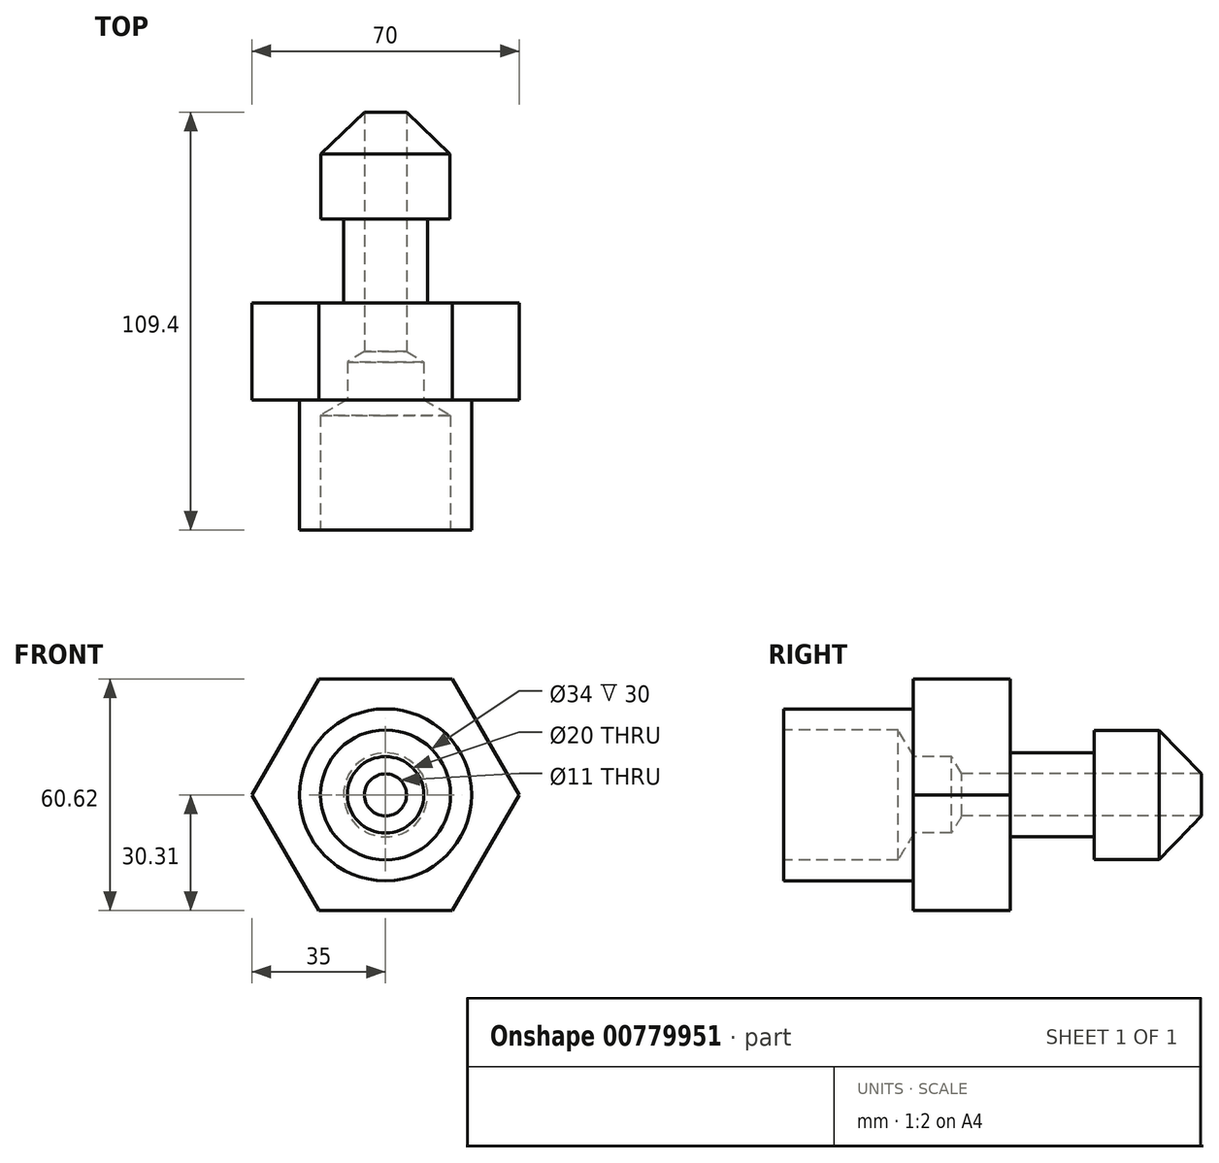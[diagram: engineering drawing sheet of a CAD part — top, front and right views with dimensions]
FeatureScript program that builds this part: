
annotation { "Feature Type Name" : "Feature", "Feature Type Description" : "" }
export const myFeature = defineFeature(function(context is Context, id is Id, definition is map)
    precondition{}
    {
        {
            var Q0;
            Q0=qCreatedBy(makeId("Front.planeOp"),FACE);
            var sketch = newSketch(context, id + "F0", { "sketchPlane" : qUnion([Q0])});
            skCircle(sketch, "E0", {"center": v(0, 0) * mm, "radius": 5.5 * mm});
            skSolve(sketch);
        }
        {
            var Q0;
            Q0=makeQuery(id+"F0.imprint","IMPRINT",FACE,{"disambiguationData":[TD([[makeQuery(id+"F0.imprint","IMPRINT",EDGE,{"derivedFrom":sQuery(id+"F0.wireOp",EDGE,"E0")}),1.0]])]});
            extrude(context, id + "F1", {"entities" : qUnion([Q0]), "depth" : 11 * mm, "offsetDistance" : 25.4 * mm, "hasDraft" : true, "draftAngle" : 46 * degree});
        }
        {
            var Q0;
            Q0=makeQuery(id+"F1.opExtrude","CAP_FACE",FACE,{"disambiguationData":[OSD([sQuery(id+"F0.wireOp",EDGE,"E0")])],"isStart":false});
            var sketch = newSketch(context, id + "F2", { "sketchPlane" : qUnion([Q0])});
            skCircle(sketch, "E1", {"center": v(0, 0) * mm, "radius": 17 * mm});
            skSolve(sketch);
        }
        {
            var Q0;
            Q0=makeQuery(id+"F2.imprint","IMPRINT",FACE,{"disambiguationData":[TD([[makeQuery(id+"F2.imprint","IMPRINT",EDGE,{"derivedFrom":makeQuery(id+"F1.opExtrude","CAP_EDGE",EDGE,{"disambiguationData":[OSD([sQuery(id+"F0.wireOp",EDGE,"E0")])],"isStart":false})}),1.0]])]});
            extrude(context, id + "F3", {"entities" : qUnion([Q0]), "operationType" : NewBodyOperationType.ADD, "depth" : 17 * mm, "offsetDistance" : 25.4 * mm});
        }
        {
            var Q0;
            Q0=makeQuery(id+"F3.opExtrude","CAP_FACE",FACE,{"disambiguationData":[OSD([sQuery(id+"F0.wireOp",EDGE,"E0")])],"isStart":false});
            var sketch = newSketch(context, id + "F4", { "sketchPlane" : qUnion([Q0])});
            skCircle(sketch, "E2", {"center": v(0, 0) * mm, "radius": 11 * mm});
            skSolve(sketch);
        }
        {
            var Q0;
            Q0=makeQuery(id+"F4.imprint","IMPRINT",FACE,{"disambiguationData":[TD([[makeQuery(id+"F4.imprint","IMPRINT",EDGE,{"derivedFrom":sQuery(id+"F4.wireOp",EDGE,"E2")}),1.0]])]});
            extrude(context, id + "F5", {"entities" : qUnion([Q0]), "operationType" : NewBodyOperationType.ADD, "depth" : 22 * mm, "offsetDistance" : 25.4 * mm});
        }
        {
            var Q0;
            Q0=makeQuery(id+"F5.opExtrude","CAP_FACE",FACE,{"disambiguationData":[OSD([sQuery(id+"F4.wireOp",EDGE,"E2")])],"isStart":false});
            var sketch = newSketch(context, id + "F6", { "sketchPlane" : qUnion([Q0])});
            skCircle(sketch, "E3.cCircle", {"center": v(0, 0) * mm, "radius": 30.31 * mm, "construction": true});
            skLineSegment(sketch, "E3.0", {"start": v(35, 0) * mm, "end": v(17.5, -30.31) * mm});
            skLineSegment(sketch, "E3.1", {"start": v(17.5, -30.31) * mm, "end": v(-17.5, -30.31) * mm});
            skLineSegment(sketch, "E3.2", {"start": v(-17.5, -30.31) * mm, "end": v(-35, 0) * mm});
            skLineSegment(sketch, "E3.3", {"start": v(-35, 0) * mm, "end": v(-17.5, 30.31) * mm});
            skLineSegment(sketch, "E3.4", {"start": v(-17.5, 30.31) * mm, "end": v(17.5, 30.31) * mm});
            skLineSegment(sketch, "E3.5", {"start": v(17.5, 30.31) * mm, "end": v(35, 0) * mm});
            skPoint(sketch, "E3.0.midPoint", {"position": v(26.25, -15.16) * mm});
            skSolve(sketch);
        }
        {
            var Q0;
            Q0=makeQuery(id+"F6.imprint","IMPRINT",FACE,{"disambiguationData":[TD([[makeQuery(id+"F6.imprint","IMPRINT",EDGE,{"derivedFrom":sQuery(id+"F6.wireOp",EDGE,"E3.0")}),-1.0]])]});
            var Q1;
            Q1=makeQuery(id+"F6.imprint","IMPRINT",FACE,{"disambiguationData":[TD([[makeQuery(id+"F6.imprint","IMPRINT",EDGE,{"derivedFrom":makeQuery(id+"F5.opExtrude","CAP_EDGE",EDGE,{"disambiguationData":[OSD([sQuery(id+"F4.wireOp",EDGE,"E2")])],"isStart":false})}),1.0]])]});
            extrude(context, id + "F7", {"entities" : qUnion([Q0, Q1]), "operationType" : NewBodyOperationType.ADD, "depth" : 25.4 * mm, "offsetDistance" : 25.4 * mm});
        }
        {
            var Q0;
            Q0=makeQuery(id+"F7.opExtrude","CAP_FACE",FACE,{"disambiguationData":[OSD([sQuery(id+"F6.wireOp",EDGE,"E3.0"),sQuery(id+"F6.wireOp",EDGE,"E3.1"),sQuery(id+"F6.wireOp",EDGE,"E3.2"),sQuery(id+"F6.wireOp",EDGE,"E3.3"),sQuery(id+"F6.wireOp",EDGE,"E3.4"),sQuery(id+"F6.wireOp",EDGE,"E3.5")])],"isStart":false});
            var sketch = newSketch(context, id + "F8", { "sketchPlane" : qUnion([Q0])});
            skCircle(sketch, "E4", {"center": v(0, 0) * mm, "radius": 22.5 * mm});
            skCircle(sketch, "E5", {"center": v(0, 0) * mm, "radius": 5.5 * mm});
            skSolve(sketch);
        }
        {
            var Q0;
            Q0=makeQuery(id+"F8.imprint","IMPRINT",FACE,{"disambiguationData":[TD([[makeQuery(id+"F8.imprint","IMPRINT",EDGE,{"derivedFrom":sQuery(id+"F8.wireOp",EDGE,"E4")}),1.0]])]});
            var Q1;
            Q1=makeQuery(id+"F8.imprint","IMPRINT",FACE,{"disambiguationData":[TD([[makeQuery(id+"F8.imprint","IMPRINT",EDGE,{"derivedFrom":sQuery(id+"F8.wireOp",EDGE,"E5")}),1.0]])]});
            extrude(context, id + "F9", {"entities" : qUnion([Q0, Q1]), "operationType" : NewBodyOperationType.ADD, "depth" : 34 * mm, "offsetDistance" : 25.4 * mm, "hasDraft" : true, "draftAngle" : 0 * degree});
        }
        {
            var Q0;
            Q0=makeQuery(id+"F9.opExtrude","CAP_FACE",FACE,{"disambiguationData":[OSD([sQuery(id+"F8.wireOp",EDGE,"E4")])],"isStart":false});
            var sketch = newSketch(context, id + "F10", { "sketchPlane" : qUnion([Q0])});
            skCircle(sketch, "E6", {"center": v(0, 0) * mm, "radius": 17 * mm});
            skSolve(sketch);
        }
        {
            var Q0;
            Q0=sQuery(id+"F10.wireOp",VERTEX,"E6.center");
            var Q1;
            Q1=makeQuery(id+"F1.opExtrude","SWEPT_BODY",BODY,{"disambiguationData":[OSD([sQuery(id+"F0.wireOp",EDGE,"E0")])]});
            hole(context, id + "F11", {"style" : HoleStyle.SIMPLE, "endStyle" : HoleEndStyle.BLIND, "standardTappedOrClearance" : lookupTablePath({ "standard" : "ISO", "size" : "34", "type" : "Drilled" }), "standardBlindInLast" : lookupTablePath({ "standard" : "ISO", "size" : "34", "type" : "Drilled" }), "holeDiameter" : 34 * mm, "majorDiameter" : 6.35 * mm, "holeDepth" : 30 * mm, "isTappedThrough" : true, "tappedDepth" : 12.7 * mm, "tapClearance" : 3, "locations" : qUnion([Q0]), "scope" : qUnion([Q1])});
        }
        {
            var Q0;
            Q0=sQuery(id+"F10.wireOp",VERTEX,"E6.center");
            var Q1;
            Q1=makeQuery(id+"F1.opExtrude","SWEPT_BODY",BODY,{"disambiguationData":[OSD([sQuery(id+"F0.wireOp",EDGE,"E0")])]});
            hole(context, id + "F12", {"style" : HoleStyle.C_SINK, "endStyle" : HoleEndStyle.BLIND, "standardTappedOrClearance" : lookupTablePath({ "standard" : "ISO", "size" : "20", "type" : "Drilled" }), "standardBlindInLast" : lookupTablePath({ "standard" : "ISO", "size" : "20", "type" : "Drilled" }), "holeDiameter" : 20 * mm, "cSinkDiameter" : 34 * mm, "cSinkAngle" : 46 * degree, "majorDiameter" : 6.35 * mm, "holeDepth" : 44 * mm, "isTappedThrough" : true, "tappedDepth" : 12.7 * mm, "tapClearance" : 3, "locations" : qUnion([Q0]), "scope" : qUnion([Q1])});
        }
        {
            var Q0;
            Q0=sQuery(id+"F10.wireOp",VERTEX,"E6.center");
            var Q1;
            Q1=makeQuery(id+"F1.opExtrude","SWEPT_BODY",BODY,{"disambiguationData":[OSD([sQuery(id+"F0.wireOp",EDGE,"E0")])]});
            hole(context, id + "F13", {"style" : HoleStyle.SIMPLE, "endStyle" : HoleEndStyle.BLIND, "holeDiameter" : 11 * mm, "majorDiameter" : 6.35 * mm, "holeDepth" : 65 * mm, "isTappedThrough" : true, "tappedDepth" : 12.7 * mm, "tapClearance" : 3, "locations" : qUnion([Q0]), "scope" : qUnion([Q1])});
        }
    });
